# Revit family: 3000.109 & 110 DPJ 65x65
name_source: partatom
category: Plumbing Fixtures
units: mm (PartAtom-declared; Revit-internal decimal feet)

## family parameters
Always vertical = Yes
Cut with Voids When Loaded = No
OmniClass Number = 23.45.00.00
Part Type = Normal
Room Calculation Point = No
Round Connector Dimension = Use Diameter
Shared = No
Work Plane-Based = No

## types (2) — shared parameters
CW Connection = No
Connector Diameter = 65 mm  [stored 0.213255 ft]
HW Connection = No
Manufacturer = Aquanight Industries Ltd
URL = www.aquaknight.co.nz
Vent Connection = No
Waste Connection = Yes

## per-type parameters (varying)
| type | Description | Inlet | Model | NV | V |
| DPJ 65x65v | DownPipe Junction 65x65 vented | 26 mm | 3000.109 | No | Yes |
| DPJ 65x65nv | DownPipe Junction 65x65 non-vented | 31 mm | 3000.110 | Yes | No |

note: [stored X ft] marks values corroborated as IEEE doubles in the binary element streams (Revit-internal decimal feet)

## geometry (parser evidence)
native form markers: Blend x2, Sweep x3
no freeform markers — native parametric forms only
